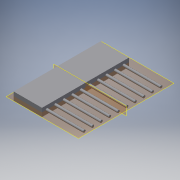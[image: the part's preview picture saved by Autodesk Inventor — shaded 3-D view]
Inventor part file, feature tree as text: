
AUTODESK INVENTOR PART (.ipt)
format: ipt  version: 2019.4 (Build 234330000, 330)  size: 137,728 bytes
history: native  units: mm
features: extrude x3, sketch x3, plane x2, pattern_linear x1, projected_geometry x1
ambient origin geometry x8: Origin, YZ Plane, XZ Plane, XY Plane, X Axis, Y Axis, Z Axis, Center Point
bodies: Solid1 (feature_tree)
feature tree (10):
  extrude  "Extrusion1"  Depth=25.84mm
  extrude  "Extrusion2"  Depth=8.43mm
  extrude  "Extrusion3"  Depth=11.15mm TaperAngle=0.0deg
  pattern_linear  "Rectangular Pattern1"  Count1=10 Spacing1=2.54mm
  plane  "Work Plane1"
  plane  "Work Plane3"
  sketch  "Sketch1"  dims[d0=2.37mm d1=25.84mm]
  sketch  "Sketch2"  dims[d2=8.43mm d3=0.0mm d4=0.75mm]
  projected_geometry  "Projected Loop1"
  sketch  "Sketch3"  dims[d5=1.45mm d6=11.15mm d7=0.0mm d8=100.0mm d10=2.54mm d11=7.0mm d12=0.0mm]
